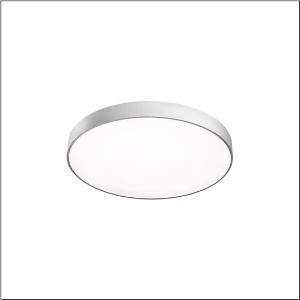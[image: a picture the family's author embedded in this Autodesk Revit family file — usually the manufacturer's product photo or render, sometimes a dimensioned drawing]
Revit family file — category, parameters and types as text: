
# Revit family: round_21_m_51mr36fd0321s
name_source: partatom
category: Lighting Fixtures
units: mm (PartAtom-declared; Revit-internal decimal feet)

## family parameters
Cut with Voids When Loaded = No
Host = Face
Light Source = No
Part Type = Normal
Room Calculation Point = No
Round Connector Dimension = Use Diameter
Shared = No

## types (1)
- Round 21 M (1 x LED, 6790 lm, 54.8 W, 3000K)
    Apparent Load = 55 VA
    CIE Flux Codes = 49 80 96 100 100
    Color Rendering = 80
    Color Temperature = 3000K
    Default Elevation = 1800 mm
    Description = Round 21 M, wall and ceiling luminaire, primary optical cover: cover, of PMMA, opal, light emission: direct distribution, primary light characteristic: symmetric, installation type: suspended mounting, surface-mounted, LED, rated luminous flux: 6.790lm, luminous efficacy: 124lm/W, light colour: 830, colour temperature: 3000K, with terminal, 5-pole, mains connection: 230V, AC, 50/60Hz, rated input power: 55W, housing, of aluminium, coated, silver, diameter: 600mm, height: 62mm, protection rating (complete): IP40, insulation class (complete): insulation class I (protective earthing), certification: CE, impact resistance: IK04, permissible operating ambient temperature: -10..+35°C, packaging unit: 1 piece
    Height = 87 mm
    Lamp = 1 x LED
    Lamp Light Flux = 6790 lm
    Lamp Power = 54.8 W
    Lamp count = 1
    Length = 600 mm
    Luminous efficacy = 124 lm/W
    Manufacturer = Siteco
    ModVariant = No
    Model = 51MR36FD0321S
    Mounting Place = Ceiling
    Mounting Type = Surface mounted
    Number of Poles = 1
    OnlyDefault = Yes
    Power Factor = 1
    Product Name = Round 21 M
    Product group = wall and ceiling luminaire
    ProductGroupID = 302
    Protection Class = Protection class I
    Protection Degree = IP 40
    RLX_Detail_Level = 1
    RLX_Emergency_Light_Flux = 0 lm
    RLX_Emergency_Type = 0
    RLX_Emergency_Type_DB = No
    RlxData = <blob elided: 14785 chars, md5=9b016e53>
    Socket = socket
    Standby Power = 0 W
    System Light Flux = 6790 lm
    System Power = 55 W
    Type Comments = Product without accessories
    Type Image = l_1258303.jpg
    URL = http://relux.com
    VarID = ---
    Voltage = 0 V
    Weight = 0.00 kg
    Width = 0 mm  [stored 0 ft]

note: [stored X ft] marks values corroborated as IEEE doubles in the binary element streams (Revit-internal decimal feet)

## geometry (parser evidence)
native form markers: Sweep x12
no freeform markers — native parametric forms only
